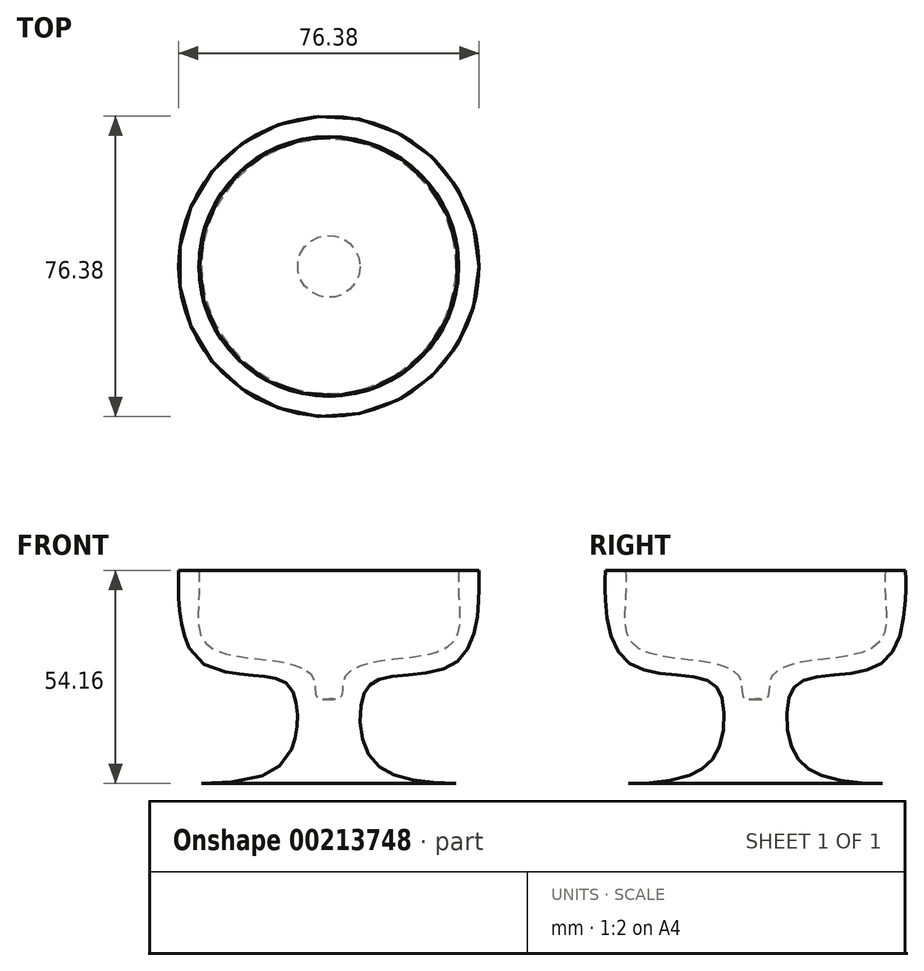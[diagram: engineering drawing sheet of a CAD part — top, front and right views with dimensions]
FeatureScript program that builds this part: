
annotation { "Feature Type Name" : "Feature", "Feature Type Description" : "" }
export const myFeature = defineFeature(function(context is Context, id is Id, definition is map)
    precondition{}
    {
        {
            var Q0;
            Q0=qCreatedBy(makeId("Front.planeOp"),FACE);
            var sketch = newSketch(context, id + "F0", { "sketchPlane" : qUnion([Q0])});
            skLineSegment(sketch, "E0", {"start": v(0, 0) * mm, "end": v(-38.13, 0) * mm});
            skFitSpline(sketch, "E1", {"points": [v(-38.13, 0) * mm, v(-11.55, 5.4) * mm, v(-8.62, 21.9) * mm, v(-14.3, 26.85) * mm, v(-32.81, 31.07) * mm, v(-38.13, 47.57) * mm, v(-38.13, 54.16) * mm], "startDerivative": vector(143.85, -0.81) * mm, "endDerivative": vector(1.6, 48.8) * mm});
            skLineSegment(sketch, "E2", {"start": v(-38.13, 54.16) * mm, "end": v(-33, 54.16) * mm});
            skFitSpline(sketch, "E3", {"points": [v(-33, 54.16) * mm, v(-33, 47.38) * mm, v(-31.34, 35.65) * mm, v(-13.38, 31.07) * mm, v(-3.85, 26.67) * mm, v(-3.12, 21.9) * mm, v(0, 21.54) * mm], "startDerivative": vector(1.78, -40.2) * mm, "endDerivative": vector(38.71, 5.07) * mm});
            skLineSegment(sketch, "E4", {"start": v(0, 21.54) * mm, "end": v(0, 0) * mm});
            skSolve(sketch);
        }
        {
            var Q0;
            {var subQ0=sQuery(id+"F0.wireOp",EDGE,"E2");Q0=makeQuery(id+"F0.imprint","IMPRINT",FACE,{"disambiguationData":[TD([[makeQuery(id+"F0.imprint","IMPRINT",EDGE,{"derivedFrom":subQ0}),-1.0]])]});}
            var Q1;
            Q1=sQuery(id+"F0.wireOp",EDGE,"E4");
            revolve(context, id + "F1", {"entities" : qUnion([Q0]), "axis" : qUnion([Q1]), "revolveType" : RevolveType.FULL});
        }
    });
